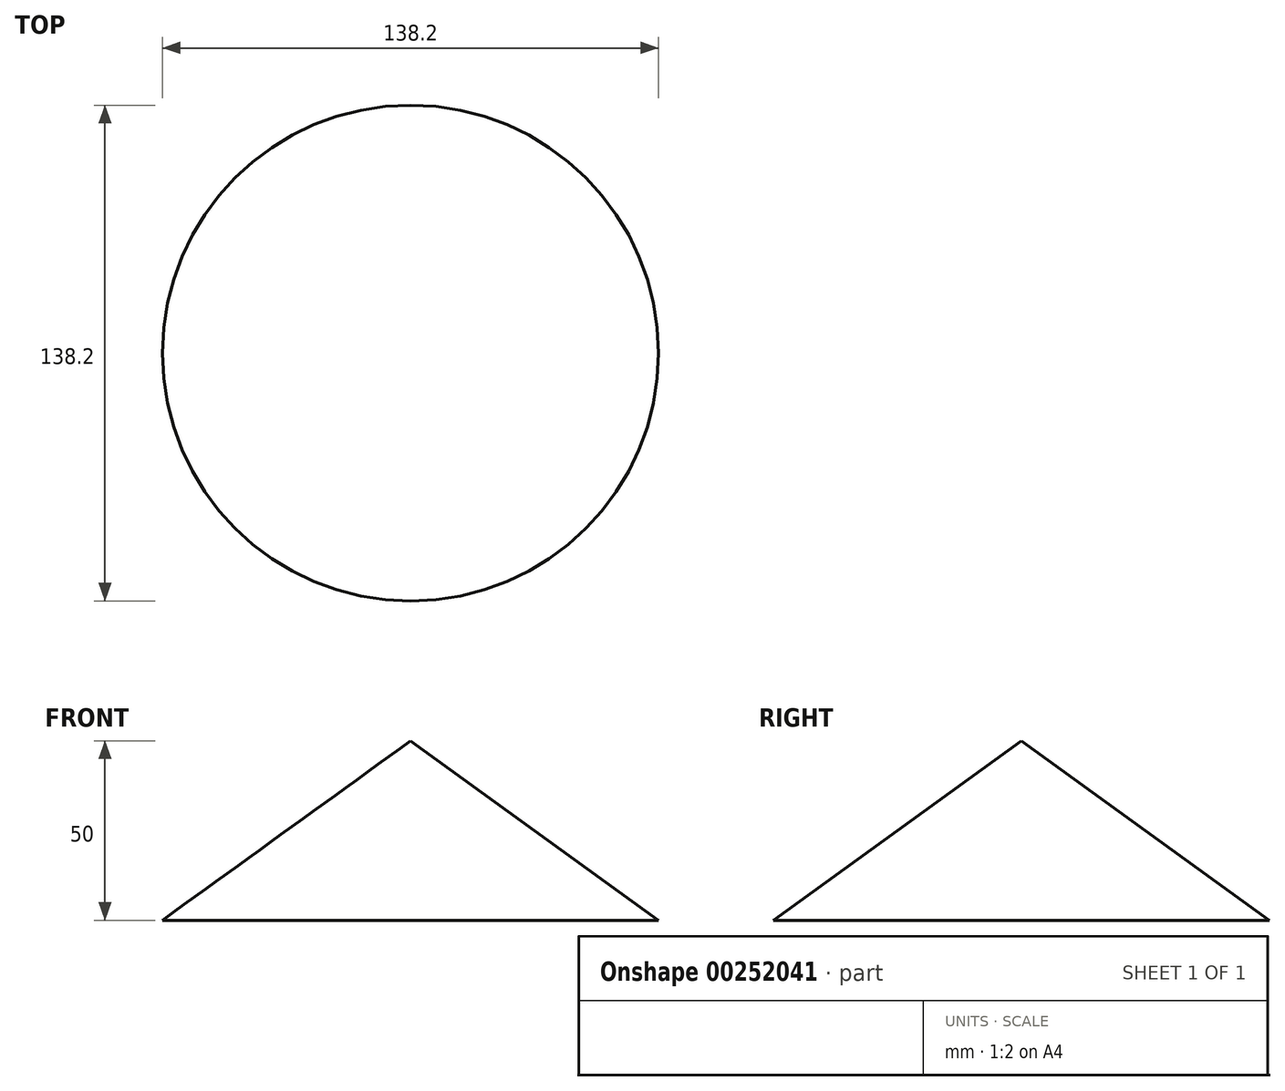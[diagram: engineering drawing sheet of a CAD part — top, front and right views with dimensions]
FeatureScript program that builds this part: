
annotation { "Feature Type Name" : "Feature", "Feature Type Description" : "" }
export const myFeature = defineFeature(function(context is Context, id is Id, definition is map)
    precondition{}
    {
        {
            var Q0;
            Q0=qCreatedBy(makeId("Front.planeOp"),FACE);
            var sketch = newSketch(context, id + "F0", { "sketchPlane" : qUnion([Q0])});
            skLineSegment(sketch, "E0", {"start": v(0, 0) * mm, "end": v(0, 50) * mm});
            skLineSegment(sketch, "E1", {"start": v(0, 50) * mm, "end": v(69.1, 0) * mm});
            skLineSegment(sketch, "E2", {"start": v(69.1, 0) * mm, "end": v(0, 0) * mm});
            skSolve(sketch);
        }
        {
            var Q0;
            Q0 = qSketchRegion(id + "F0", true);
            var Q1;
            Q1=sQuery(id+"F0.wireOp",EDGE,"E0");
            revolve(context, id + "F1", {"entities" : qUnion([Q0]), "axis" : qUnion([Q1]), "revolveType" : RevolveType.FULL});
        }
    });
